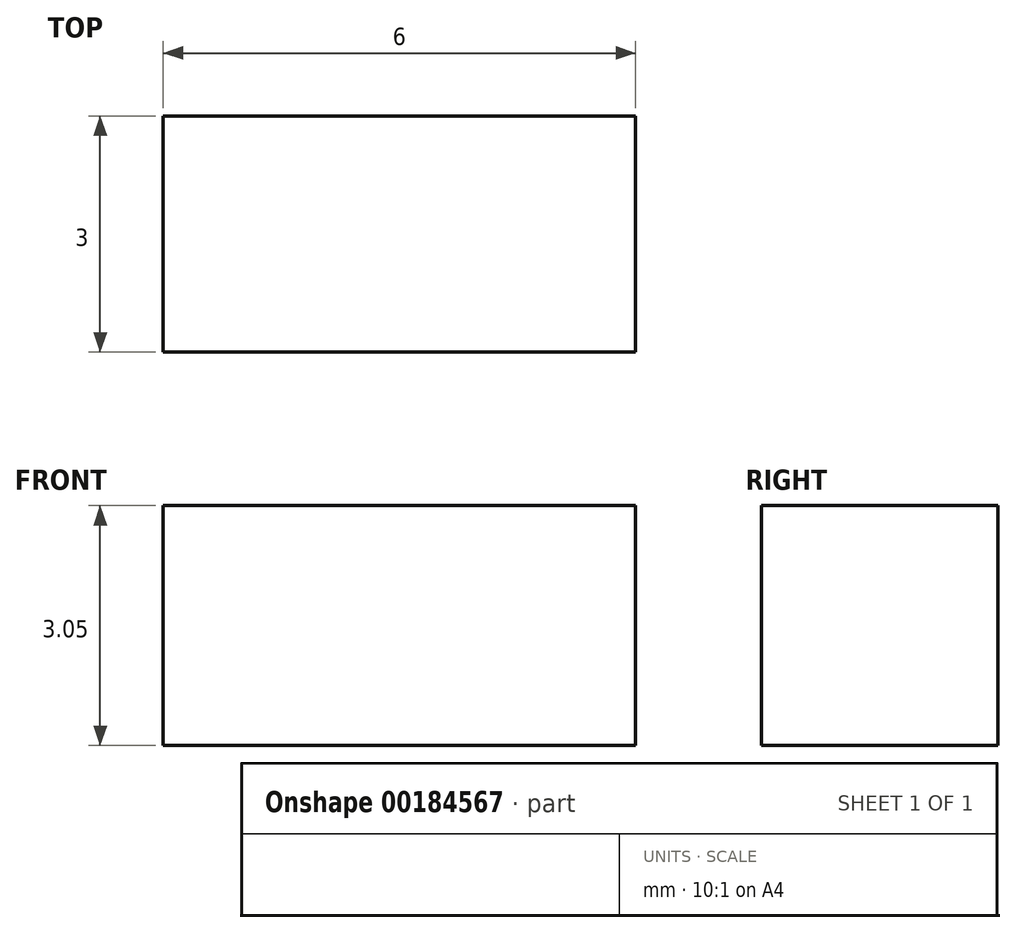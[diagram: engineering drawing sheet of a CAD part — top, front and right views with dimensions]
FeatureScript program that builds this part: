
annotation { "Feature Type Name" : "Feature", "Feature Type Description" : "" }
export const myFeature = defineFeature(function(context is Context, id is Id, definition is map)
    precondition{}
    {
        {
            var Q0;
            Q0=qCreatedBy(makeId("Front.planeOp"),FACE);
            var sketch = newSketch(context, id + "F0", { "sketchPlane" : qUnion([Q0])});
            skLineSegment(sketch, "E0.bottom", {"start": v(0, 0) * mm, "end": v(6, 0) * mm});
            skLineSegment(sketch, "E0.top", {"start": v(0, 3.05) * mm, "end": v(6, 3.05) * mm});
            skLineSegment(sketch, "E0.left", {"start": v(0, 0) * mm, "end": v(0, 3.05) * mm});
            skLineSegment(sketch, "E0.right", {"start": v(6, 0) * mm, "end": v(6, 3.05) * mm});
            skSolve(sketch);
        }
        {
            var Q0;
            Q0=qSketchRegion(id+"F0",true);
            extrude(context, id + "F1", {"entities" : qUnion([Q0]), "depth" : 3 * mm});
        }
    });
